# Revit family: Shower_Rose_Nero_Opal
name_source: partatom
category: Plumbing Fixtures
units: mm (PartAtom-declared; Revit-internal decimal feet)

## family parameters
Always vertical = Yes
Cut with Voids When Loaded = Yes
Maintain Annotation Orientation = No
OmniClass Number = 23.31.17.00
Part Type = Normal
Room Calculation Point = No
Round Connector Dimension = Use Diameter
Shared = No
Work Plane-Based = No

## types (7) — shared parameters
Assembly Code = D2010710
CW Connection = Yes
HW Connection = Yes
IfcExportAs = IfcSanitaryTerminal
IfcExportType = SHOWER
Manufacturer = Nero
ManufacturerOverallDepth = 250 mm
ManufacturerOverallHeight = 682.5 mm  [stored 2.23917 ft]
ManufacturerOverallWidth = 250 mm
ManufacturerURLProductSpecific = https://nerotapware.com.au
ModifiedIssue = 20241210 $
URL = https://nerotapware.com.au
Uniclass2015Code = Pr_40_20_87_75
Uniclass2015Title = Shower fittings package
Vent Connection = No
Waste Connection = No
zero-valued in all types: Default Elevation

## per-type parameters (varying)
| type | BodyMaterial | Description | ManufacturerSpecCode | Model | Type Comments | Uniclass2015Version |
| Brushed Bronze (NR508079BZ) | Metal_Bronze_Nero_Brushed | Opal 250mm Shower Head Brushed Bronze | NR508079BZ | NR508079BZ | Shower - Rose - Brushed Bronze | Products v1.28 |
| Chrome (NR508079CH) | Metal_Chrome_Nero | Opal 250mm Shower Head Chrome | NR508079CH | NR508079CH | Shower - Rose - Chrome | Products v1.35 |
| Matte Black (NR508079MB) | Metal_MatteBlack_Nero | Opal 250mm Shower Head Matte Black | NR508079MB | NR508079MB | Shower - Rose - Matte Black | Products v1.28 |
| Gun Metal (NR508079GM) | Metal_GunMetal_Nero | Opal 250mm Shower Head Gun Metal | NR508079GM | NR508079GM | Shower - Rose - Gun Metal | Products v1.35 |
| Graphite (NR508079GR) | Metal_Graphite_Nero_Brushed | Opal 250mm Shower Head Graphite | NR508079GR | NR508079GR | Shower - Rose - Graphite | Products v1.28 |
| Brushed Gold (NR508079BG) | Metal_Gold_Nero_Brushed | Opal 250mm Shower Head Brushed Gold | NR508079BG | NR508079BG | Shower - Rose - Brushed Gold | Products v1.28 |
| Brushed Nickel (NR508079BN) | Metal_Nickel_Nero_Brushed | Opal 250mm Shower Head Brushed Nickel | NR508079BN | NR508079BN | Shower - Rose - Brushed Nickel | Products v1.28 |

note: [stored X ft] marks values corroborated as IEEE doubles in the binary element streams (Revit-internal decimal feet)

## geometry (parser evidence)
native form markers: Sweep x3
no freeform markers — native parametric forms only
